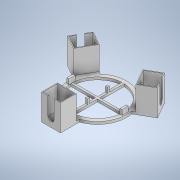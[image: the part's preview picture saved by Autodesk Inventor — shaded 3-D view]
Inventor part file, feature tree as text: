
AUTODESK INVENTOR PART (.ipt)
format: ipt  version: 2020 (Build 240168000, 168)  size: 248,832 bytes
history: native  units: mm
features: extrude x4, sketch x4, pattern_circular x1
ambient origin geometry x8: Origin, YZ Plane, XZ Plane, XY Plane, X Axis, Y Axis, Z Axis, Center Point
bodies: Solid1 (feature_tree)
feature tree (9):
  extrude  "Extrusion1"  Depth=100.0mm
  extrude  "Extrusion2"  Depth=4.0mm
  extrude  "Extrusion3"  Depth=100.0mm
  pattern_circular  "Circular Pattern1"  Count=6  [1 undecoded]
  extrude  "Extrusion4"  Depth=31.0mm
  sketch  "Sketch1"  dims[d0=114.0mm d1=100.0mm]
  sketch  "Sketch2"  dims[d6=100.0mm d7=4.0mm]
  sketch  "Sketch4"  dims[d8=4.0mm d9=100.0mm]
  sketch  "Sketch5"  dims[d10=37.0mm d14=60.0mm d15=31.0mm d16=30.0mm d18=360.0deg d20=5.0mm d21=0.0mm d22=31.0mm d23=1.5mm d24=30.0mm d26=360.0deg d28=46.0mm d29=0.0mm d30=30.0mm d31=360.0deg d36=12.0mm d37=5.0mm d38=6.0mm d39=46.0mm d40=0.0mm d41=17.5mm d42=4.0mm d43=12.0mm d44=10.0mm d45=0.0mm]
note: 1 required parameter value undecoded (feature->parameter linkage not recoverable at this tier; creation-order binding heuristic only, values carry confidence <= 0.55)
